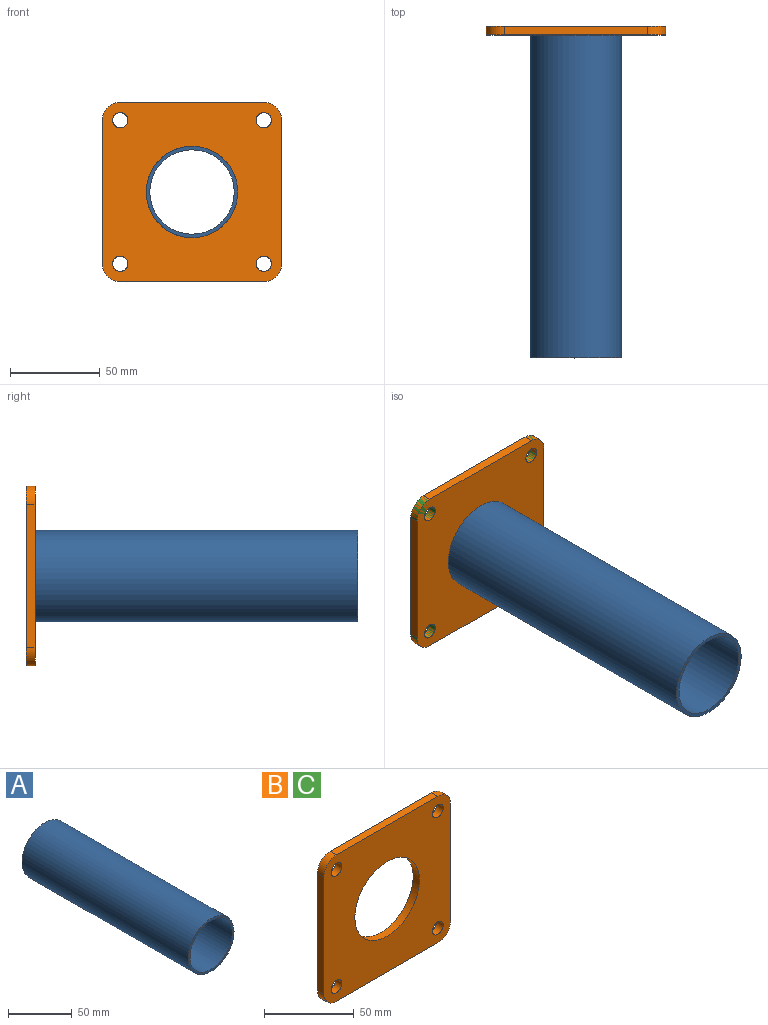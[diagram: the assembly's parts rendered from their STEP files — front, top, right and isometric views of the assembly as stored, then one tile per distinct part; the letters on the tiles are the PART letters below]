
ASSEMBLY  parts=3 mates=1
PART A: 4 faces, bbox 51x185x51 mm
  f0: cylinder r=23.5mm len=185mm, axis (0,1,0), area 27316.1mm2, adj f2,f3
  f1: cylinder r=25.5mm len=185mm, axis (0,1,0), area 29640.9mm2, adj f2,f3
  f2: plane 51x51mm, normal (0,-1,0), area 307.9mm2, adj f0,f1
  f3: plane 51x51mm, normal (0,1,0), area 307.9mm2, adj f0,f1
PART B: 15 faces, bbox 100x5x100 mm
  f0: plane 80x5mm, normal (1,0,0), area 400mm2, adj f1,f7,f8,f9
  f1: cylinder r=10mm len=10mm, axis (0,1,0), area 78.5mm2, adj f0,f2,f8,f9
  f2: plane 80x5mm, normal (0,0,1), area 400mm2, adj f1,f3,f8,f9
  f3: cylinder r=10mm len=10mm, axis (0,1,0), area 78.5mm2, adj f2,f4,f8,f9
  f4: plane 80x5mm, normal (-1,0,0), area 400mm2, adj f3,f5,f8,f9
  f5: cylinder r=10mm len=10mm, axis (0,1,0), area 78.5mm2, adj f4,f6,f8,f9
  f6: plane 80x5mm, normal (0,0,-1), area 400mm2, adj f5,f7,f8,f9
  f7: cylinder r=10mm len=10mm, axis (0,1,0), area 78.5mm2, adj f0,f6,f8,f9
  f8: plane 100x100mm, normal (0,-1,0), area 7644.4mm2, adj f0,f1,f2,f3,f4,f5,f6,f7
  f9: plane 100x100mm, normal (0,1,0), area 7644.4mm2, adj f0,f1,f2,f3,f4,f5,f6,f7
  f10: cylinder r=4.25mm len=8.5mm, axis (0,1,0), area 133.5mm2, adj f8,f9
  f11: cylinder r=4.25mm len=8.5mm, axis (0,1,0), area 133.5mm2, adj f8,f9
  f12: cylinder r=4.25mm len=8.5mm, axis (0,1,0), area 133.5mm2, adj f8,f9
  f13: cylinder r=4.25mm len=8.5mm, axis (0,1,0), area 133.5mm2, adj f8,f9
  f14: cylinder r=25.5mm len=51mm, axis (0,1,0), area 801.1mm2, adj f8,f9
PART C: same geometry as B
PLACE A t=(0.44,2.69,-0.09)mm
PLACE B t=(-49.56,2.69,-50.09)mm
PLACE C t=(-49.56,2.69,-50.09)mm
MATE fastened A.f0 <-> C.f14  axis (0,1,0) through (0.44,2.69,-0.09)mm
